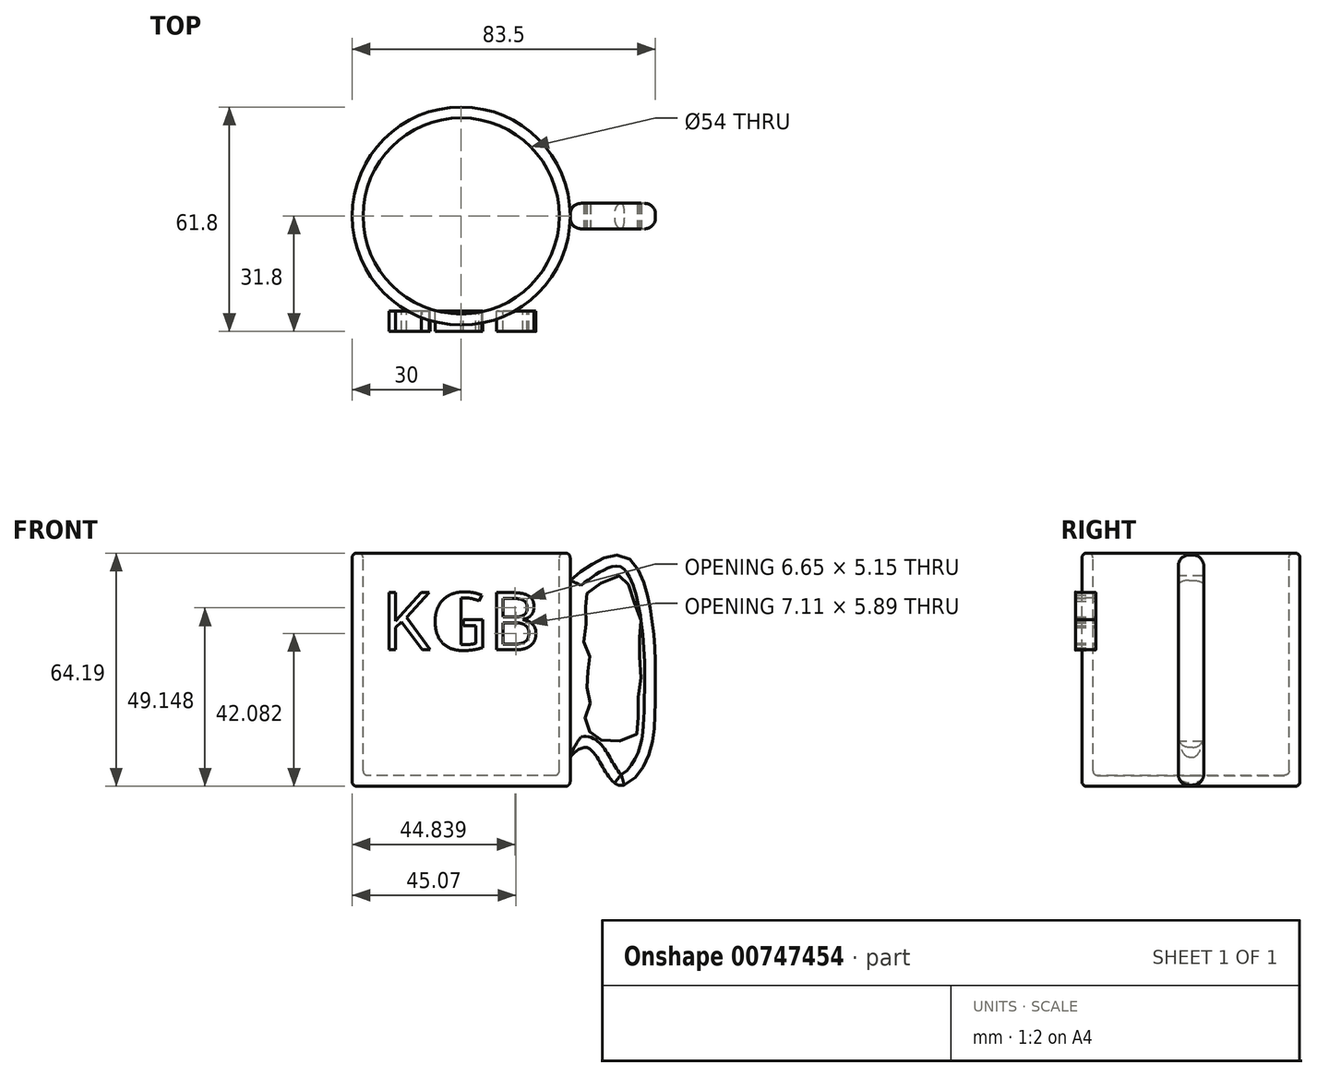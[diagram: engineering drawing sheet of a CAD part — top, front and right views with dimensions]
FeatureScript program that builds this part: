
annotation { "Feature Type Name" : "Feature", "Feature Type Description" : "" }
export const myFeature = defineFeature(function(context is Context, id is Id, definition is map)
    precondition{}
    {
        {
            var Q0;
            Q0=qCreatedBy(makeId("Front.planeOp"),FACE);
            var sketch = newSketch(context, id + "F0", { "sketchPlane" : qUnion([Q0])});
            skLineSegment(sketch, "E0.top", {"start": v(0, -45.65) * mm, "end": v(28.74, -45.65) * mm});
            skLineSegment(sketch, "E0.left", {"start": v(0, 18.34) * mm, "end": v(0, -45.65) * mm});
            skLineSegment(sketch, "E0.right", {"start": v(30, 17.28) * mm, "end": v(30, -44.4) * mm});
            skLineSegment(sketch, "E1.1", {"start": v(3, -42.65) * mm, "end": v(25.74, -42.65) * mm});
            skLineSegment(sketch, "E1.2", {"start": v(27, 17.28) * mm, "end": v(27, -41.4) * mm});
            skLineSegment(sketch, "E2", {"start": v(3, -42.65) * mm, "end": v(0, -42.65) * mm});
            skLineSegment(sketch, "E3", {"start": v(28.26, 18.54) * mm, "end": v(28.74, 18.54) * mm});
            skPoint(sketch, "E4.visualSharp", {"position": v(30, 18.54) * mm});
            skArc(sketch, "E4.filletArc", {"start": v(30, 17.28) * mm, "mid": v(29.63, 18.17) * mm, "end": v(28.74, 18.54) * mm});
            skPoint(sketch, "E5.visualSharp", {"position": v(27, 18.54) * mm});
            skArc(sketch, "E5.filletArc", {"start": v(28.26, 18.54) * mm, "mid": v(27.37, 18.17) * mm, "end": v(27, 17.28) * mm});
            skPoint(sketch, "E6.visualSharp", {"position": v(27, -42.65) * mm});
            skArc(sketch, "E6.filletArc", {"start": v(25.74, -42.65) * mm, "mid": v(26.63, -42.28) * mm, "end": v(27, -41.4) * mm});
            skPoint(sketch, "E7.visualSharp", {"position": v(30, -45.65) * mm});
            skArc(sketch, "E7.filletArc", {"start": v(28.74, -45.65) * mm, "mid": v(29.63, -45.28) * mm, "end": v(30, -44.4) * mm});
            skSolve(sketch);
        }
        {
            var Q0;
            {var subQ1=sQuery(id+"F0.wireOp",EDGE,"E0.top");Q0=makeQuery(id+"F0.imprint","IMPRINT",FACE,{"disambiguationData":[TD([[makeQuery(id+"F0.imprint","IMPRINT",EDGE,{"derivedFrom":subQ1}),1.0]])]});}
            var Q1;
            Q1=sQuery(id+"F0.wireOp",EDGE,"E0.left");
            revolve(context, id + "F1", {"surfaceOperationType" : NewSurfaceOperationType.NEW, "entities" : qUnion([Q0]), "axis" : qUnion([Q1]), "revolveType" : RevolveType.FULL});
        }
        {
            var Q0;
            Q0=qCreatedBy(makeId("Front.planeOp"),FACE);
            var sketch = newSketch(context, id + "F2", { "sketchPlane" : qUnion([Q0])});
            skFitSpline(sketch, "E8", {"points": [v(30, 11.06) * mm, v(45.47, 17.42) * mm, v(52.83, -2.12) * mm, v(53.4, -22.52) * mm, v(50.85, -38.95) * mm, v(42.92, -45.18) * mm, v(35.27, -35.27) * mm, v(30, -37.62) * mm], "startDerivative": vector(106.77, 91.58) * mm, "endDerivative": vector(-52.43, -58.16) * mm});
            skLineSegment(sketch, "E9", {"start": v(30, 11.06) * mm, "end": v(30, -37.62) * mm});
            skSolve(sketch);
        }
        {
            var Q0;
            Q0=makeQuery(id+"F2.imprint","IMPRINT",FACE,{"disambiguationData":[TD([[makeQuery(id+"F2.imprint","IMPRINT",EDGE,{"derivedFrom":sQuery(id+"F2.wireOp",EDGE,"E8")}),-1.0]])]});
            extrude(context, id + "F3", {"entities" : qUnion([Q0]), "endBound" : BoundingType.SYMMETRIC, "depth" : 7 * mm, "offsetDistance" : 25 * mm});
        }
        {
            var Q0;
            Q0=makeQuery(id+"F3.opExtrude","CAP_EDGE",EDGE,{"disambiguationData":[OSD([sQuery(id+"F2.wireOp",EDGE,"E8")])],"isStart":false});
            var Q1;
            Q1=makeQuery(id+"F3.opExtrude","CAP_EDGE",EDGE,{"disambiguationData":[OSD([sQuery(id+"F2.wireOp",EDGE,"E8")])],"isStart":true});
            var Q2;
            Q2=makeQuery(id+"F3.opExtrude","CAP_FACE",FACE,{"disambiguationData":[OSD([sQuery(id+"F2.wireOp",EDGE,"E8"),sQuery(id+"F2.wireOp",EDGE,"E9")])],"isStart":true});
            var Q3;
            Q3=makeQuery(id+"F3.opExtrude","CAP_EDGE",EDGE,{"disambiguationData":[OSD([sQuery(id+"F2.wireOp",EDGE,"E9")])],"isStart":false});
            var Q4;
            Q4=makeQuery(id+"F3.opExtrude","CAP_EDGE",EDGE,{"disambiguationData":[OSD([sQuery(id+"F2.wireOp",EDGE,"E9")])],"isStart":true});
            fillet(context, id + "F4", {"entities" : qUnion([Q0, Q1, Q2, Q3, Q4]), "radius" : 3 * mm, "tangentPropagation" : true, "allowEdgeOverflow" : false});
        }
        {
            var Q0;
            Q0=makeQuery(id+"F3.opExtrude","CAP_FACE",FACE,{"disambiguationData":[OSD([sQuery(id+"F2.wireOp",EDGE,"E8"),sQuery(id+"F2.wireOp",EDGE,"E9")])],"isStart":false});
            var sketch = newSketch(context, id + "F5", { "sketchPlane" : qUnion([Q0])});
            skFitSpline(sketch, "E10", {"points": [v(37.41, 9.57) * mm, v(34.13, 6.2) * mm, v(34.63, 0.73) * mm, v(33.79, -6.1) * mm, v(35.64, -11.06) * mm, v(34.3, -16.53) * mm, v(35.56, -22.26) * mm, v(34.04, -27.23) * mm, v(36.23, -31.6) * mm, v(40.61, -33.3) * mm, v(48.36, -31.27) * mm, v(48.44, -24.28) * mm, v(49.54, -15.86) * mm, v(48.86, -6.34) * mm, v(49.54, 0) * mm, v(46.76, 7.13) * mm, v(44.49, 12.18) * mm, v(37.41, 9.57) * mm]});
            skSolve(sketch);
        }
        {
            var Q0;
            {var subQ0=sQuery(id+"F5.wireOp",EDGE,"E10");var subQ1=sQuery(id+"F2.wireOp",EDGE,"E8");var subQ2=makeQuery(id+"F4.opFillet","BLEND_EDGE",EDGE,{"disambiguationData":[OD(0.0)],"blendedFrom":[makeQuery(id+"F3.opExtrude","CAP_EDGE",EDGE,{"disambiguationData":[OSD([subQ1])],"isStart":false}),makeQuery(id+"F3.opExtrude","CAP_FACE",FACE,{"disambiguationData":[OSD([subQ1,sQuery(id+"F2.wireOp",EDGE,"E9")])],"isStart":false})],"blendedInto":[makeQuery(id+"F3.opExtrude","CAP_FACE",FACE,{"disambiguationData":[OSD([subQ1,sQuery(id+"F2.wireOp",EDGE,"E9")])],"isStart":false})]});var subQ3=makeQuery(id+"F5.imprint","INTERSECT",VERTEX,{"disambiguationData":[OD(0.0)],"derivedFrom":[subQ2,subQ0]});Q0=makeQuery(id+"F5.imprint","IMPRINT",FACE,{"disambiguationData":[TD([[makeQuery(id+"F5.imprint","IMPRINT",EDGE,{"disambiguationData":[TD([[subQ3,1.0]])],"derivedFrom":subQ0}),1.0]])]});}
            extrude(context, id + "F6", {"entities" : qUnion([Q0]), "operationType" : NewBodyOperationType.REMOVE, "endBound" : BoundingType.SYMMETRIC, "oppositeDirection" : true, "depth" : 25 * mm, "offsetDistance" : 25 * mm});
        }
        {
            var Q0;
            Q0=qCreatedBy(makeId("Front.planeOp"),FACE);
            cPlane(context, id + "F7", {"entities" : qUnion([Q0]), "cplaneType" : CPlaneType.OFFSET, "offset" : 29 * mm, "width" : 150 * mm, "height" : 150 * mm});
        }
        {
            var Q0;
            Q0=qCreatedBy(id+"F7.planeOp",FACE);
            var sketch = newSketch(context, id + "F8", { "sketchPlane" : qUnion([Q0])});
            skText(sketch, "E11", { "text": "KGB", "fontName": "OpenSans-Regular.ttf"});
            skLineSegment(sketch, "E12", {"start": v(0, 7.8) * mm, "end": v(0, -8.07) * mm});
            skLineSegment(sketch, "E13", {"start": v(0, 22.6) * mm, "end": v(0, -22.06) * mm});
            const initialGuessF8  = {"E11": [-0.02203, -0.00807, 1, 0, 0.01586]};
            skSetInitialGuess(sketch, initialGuessF8);
            skSolve(sketch);
        }
        {
            var Q0;
            Q0 = qSketchRegion(id + "F8", true);
            extrude(context, id + "F9", {"entities" : qUnion([Q0]), "endBound" : BoundingType.SYMMETRIC, "depth" : 5.6 * mm, "offsetDistance" : 25 * mm});
        }
    });
